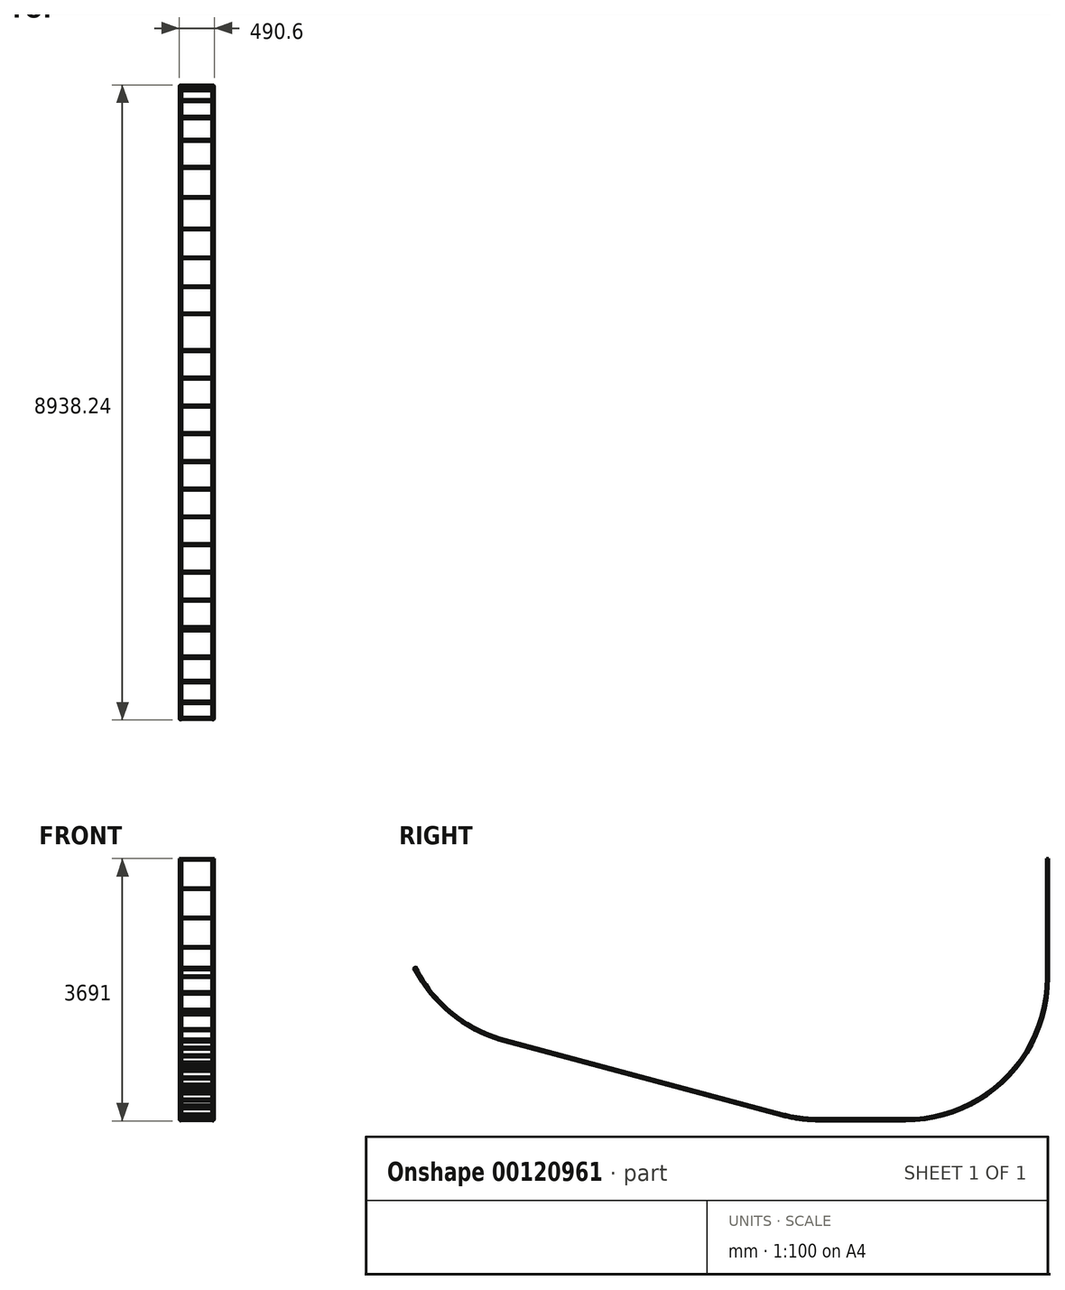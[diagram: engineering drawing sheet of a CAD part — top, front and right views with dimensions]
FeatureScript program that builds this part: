
annotation { "Feature Type Name" : "Feature", "Feature Type Description" : "" }
export const myFeature = defineFeature(function(context is Context, id is Id, definition is map)
    precondition{}
    {
        {
            var Q0;
            Q0=qCreatedBy(makeId("Right.planeOp"),FACE);
            var sketch = newSketch(context, id + "F0", { "sketchPlane" : qUnion([Q0])});
            skLineSegment(sketch, "E0", {"start": v(0, 0) * mm, "end": v(0, 1981.2) * mm, "construction": true});
            skLineSegment(sketch, "E1", {"start": v(0, 0) * mm, "end": v(-1981.2, 0) * mm, "construction": true});
            skArc(sketch, "E2", {"start": v(0, 1981.2) * mm, "mid": v(-580.28, 580.28) * mm, "end": v(-1981.2, 0) * mm});
            skLineSegment(sketch, "E3", {"start": v(0, 1981.2) * mm, "end": v(0, 3657.6) * mm});
            skLineSegment(sketch, "E4", {"start": v(-1981.2, 0) * mm, "end": v(-3200.4, 0) * mm});
            skArc(sketch, "E5", {"start": v(-3200.4, 0) * mm, "mid": v(-3459, 16.95) * mm, "end": v(-3713.17, 67.5) * mm});
            skLineSegment(sketch, "E6", {"start": v(-3713.17, 67.5) * mm, "end": v(-7620, 1114.34) * mm});
            skArc(sketch, "E7", {"start": v(-7620, 1114.34) * mm, "mid": v(-8356.22, 1490.12) * mm, "end": v(-8875.04, 2133.6) * mm});
            skLineSegment(sketch, "E8", {"start": v(-3200.4, 0) * mm, "end": v(-7620, 0) * mm, "construction": true});
            skSolve(sketch);
        }
        {
            var Q0;
            Q0=sQuery(id+"F0.wireOp",VERTEX,"E3.end");
            var Q1;
            Q1=qCreatedBy(makeId("Top.planeOp"),FACE);
            cPlane(context, id + "F1", {"entities" : qUnion([Q0, Q1]), "cplaneType" : CPlaneType.PLANE_POINT, "offset" : 25.4 * mm, "width" : 152.4 * mm, "height" : 152.4 * mm});
        }
        {
            var Q0;
            Q0=qCreatedBy(id+"F1.planeOp",FACE);
            var sketch = newSketch(context, id + "F2", { "sketchPlane" : qUnion([Q0])});
            skCircle(sketch, "E9", {"center": v(0, 16.7) * mm, "radius": 16.7 * mm});
            skCircle(sketch, "E10", {"center": v(0, 16.7) * mm, "radius": 13.32 * mm});
            skSolve(sketch);
        }
        {
            var Q0;
            Q0=makeQuery(id+"F2.imprint","IMPRINT",FACE,{"disambiguationData":[TD([[makeQuery(id+"F2.imprint","IMPRINT",EDGE,{"derivedFrom":sQuery(id+"F2.wireOp",EDGE,"E9")}),1.0]])]});
            var Q1;
            Q1=sQuery(id+"F0.wireOp",EDGE,"E3");
            var Q2;
            Q2=sQuery(id+"F0.wireOp",EDGE,"E2");
            var Q3;
            Q3=sQuery(id+"F0.wireOp",EDGE,"E4");
            var Q4;
            Q4=sQuery(id+"F0.wireOp",EDGE,"E5");
            var Q5;
            Q5=sQuery(id+"F0.wireOp",EDGE,"E6");
            var Q6;
            Q6=sQuery(id+"F0.wireOp",EDGE,"E7");
            sweep(context, id + "F3", {"profiles" : qUnion([Q0]), "path" : qUnion([Q1, Q2, Q3, Q4, Q5, Q6])});
        }
        {
            var Q0;
            Q0=qCreatedBy(makeId("Right.planeOp"),FACE);
            cPlane(context, id + "F4", {"entities" : qUnion([Q0]), "cplaneType" : CPlaneType.OFFSET, "offset" : 228.6 * mm, "oppositeDirection" : true, "width" : 152.4 * mm, "height" : 152.4 * mm});
        }
        {
            var Q0;
            Q0=qCreatedBy(id+"F4.planeOp",FACE);
            var sketch = newSketch(context, id + "F5", { "sketchPlane" : qUnion([Q0])});
            skLineSegment(sketch, "E11.0", {"start": v(0, 1981.2) * mm, "end": v(0, 3657.6) * mm, "construction": true});
            skArc(sketch, "E12.0", {"start": v(0, 1981.2) * mm, "mid": v(-580.28, 580.28) * mm, "end": v(-1981.2, 0) * mm, "construction": true});
            skLineSegment(sketch, "E13", {"start": v(-3200.4, 0) * mm, "end": v(-1981.2, 0) * mm, "construction": true});
            skArc(sketch, "E14.0", {"start": v(-3200.4, 0) * mm, "mid": v(-3459, 16.95) * mm, "end": v(-3713.17, 67.5) * mm, "construction": true});
            skLineSegment(sketch, "E15.0", {"start": v(-3713.17, 67.5) * mm, "end": v(-7620, 1114.34) * mm, "construction": true});
            skArc(sketch, "E16.0", {"start": v(-7620, 1114.34) * mm, "mid": v(-8356.22, 1490.12) * mm, "end": v(-8875.04, 2133.6) * mm, "construction": true});
            skArc(sketch, "E17.0", {"start": v(-7624.32, 1098.2) * mm, "mid": v(-8366.75, 1477.16) * mm, "end": v(-8889.94, 2126.06) * mm, "construction": true});
            skLineSegment(sketch, "E17.1", {"start": v(-3717.5, 51.38) * mm, "end": v(-7624.32, 1098.2) * mm, "construction": true});
            skLineSegment(sketch, "E17.2", {"start": v(16.7, 1981.2) * mm, "end": v(16.7, 3657.6) * mm, "construction": true});
            skArc(sketch, "E17.3", {"start": v(16.7, 1981.2) * mm, "mid": v(-568.47, 568.47) * mm, "end": v(-1981.2, -16.7) * mm, "construction": true});
            skLineSegment(sketch, "E17.4", {"start": v(-3200.4, -16.7) * mm, "end": v(-1981.2, -16.7) * mm, "construction": true});
            skArc(sketch, "E17.5", {"start": v(-3200.4, -16.7) * mm, "mid": v(-3461.18, 0.4) * mm, "end": v(-3717.5, 51.38) * mm, "construction": true});
            skLineSegment(sketch, "E18.bottom", {"start": v(4, 3657.6) * mm, "end": v(29.4, 3657.6) * mm});
            skLineSegment(sketch, "E18.top", {"start": v(4, 3632.2) * mm, "end": v(29.4, 3632.2) * mm});
            skLineSegment(sketch, "E18.left", {"start": v(4, 3657.6) * mm, "end": v(4, 3632.2) * mm});
            skLineSegment(sketch, "E18.right", {"start": v(29.4, 3657.6) * mm, "end": v(29.4, 3632.2) * mm});
            skPoint(sketch, "E18.middle", {"position": v(16.7, 3644.9) * mm});
            skLineSegment(sketch, "E19.0.1.0", {"start": v(4, 3219.45) * mm, "end": v(29.4, 3219.45) * mm});
            skLineSegment(sketch, "E19.0.1.1", {"start": v(4, 3244.85) * mm, "end": v(4, 3219.45) * mm});
            skPoint(sketch, "E19.0.1.2", {"position": v(16.7, 3232.15) * mm});
            skLineSegment(sketch, "E19.0.1.3", {"start": v(4, 3244.85) * mm, "end": v(29.4, 3244.85) * mm});
            skLineSegment(sketch, "E19.0.1.4", {"start": v(29.4, 3244.85) * mm, "end": v(29.4, 3219.45) * mm});
            skLineSegment(sketch, "E19.0.2.0", {"start": v(4, 2806.7) * mm, "end": v(29.4, 2806.7) * mm});
            skLineSegment(sketch, "E19.0.2.1", {"start": v(4, 2832.1) * mm, "end": v(4, 2806.7) * mm});
            skPoint(sketch, "E19.0.2.2", {"position": v(16.7, 2819.4) * mm});
            skLineSegment(sketch, "E19.0.2.3", {"start": v(4, 2832.1) * mm, "end": v(29.4, 2832.1) * mm});
            skLineSegment(sketch, "E19.0.2.4", {"start": v(29.4, 2832.1) * mm, "end": v(29.4, 2806.7) * mm});
            skLineSegment(sketch, "E19.0.3.0", {"start": v(4, 2393.95) * mm, "end": v(29.4, 2393.95) * mm});
            skLineSegment(sketch, "E19.0.3.1", {"start": v(4, 2419.35) * mm, "end": v(4, 2393.95) * mm});
            skPoint(sketch, "E19.0.3.2", {"position": v(16.7, 2406.65) * mm});
            skLineSegment(sketch, "E19.0.3.3", {"start": v(4, 2419.35) * mm, "end": v(29.4, 2419.35) * mm});
            skLineSegment(sketch, "E19.0.3.4", {"start": v(29.4, 2419.35) * mm, "end": v(29.4, 2393.95) * mm});
            skLineSegment(sketch, "E19.0.4.0", {"start": v(4, 1981.2) * mm, "end": v(29.4, 1981.2) * mm});
            skLineSegment(sketch, "E19.0.4.1", {"start": v(4, 2006.6) * mm, "end": v(4, 1981.2) * mm});
            skPoint(sketch, "E19.0.4.2", {"position": v(16.7, 1993.9) * mm});
            skLineSegment(sketch, "E19.0.4.3", {"start": v(4, 2006.6) * mm, "end": v(29.4, 2006.6) * mm});
            skLineSegment(sketch, "E19.0.4.4", {"start": v(29.4, 2006.6) * mm, "end": v(29.4, 1981.2) * mm});
            skLineSegment(sketch, "E19.direction1", {"start": v(4, 3632.2) * mm, "end": v(29.4, 3632.2) * mm, "construction": true});
            skLineSegment(sketch, "E19.direction2", {"start": v(4, 3632.2) * mm, "end": v(4, 3219.45) * mm, "construction": true});
            skLineSegment(sketch, "E20", {"start": v(4, 1981.2) * mm, "end": v(3.84, 1955.8) * mm});
            skLineSegment(sketch, "E21", {"start": v(3.84, 1955.8) * mm, "end": v(29.24, 1955.64) * mm});
            skLineSegment(sketch, "E22", {"start": v(29.24, 1955.64) * mm, "end": v(29.4, 1981.04) * mm});
            skLineSegment(sketch, "E23", {"start": v(29.4, 1981.04) * mm, "end": v(4, 1981.2) * mm});
            skLineSegment(sketch, "E24", {"start": v(16.7, 1981.12) * mm, "end": v(16.54, 1955.72) * mm, "construction": true});
            skLineSegment(sketch, "E25.1.0", {"start": v(-21.05, 1533.64) * mm, "end": v(-45.77, 1539.45) * mm});
            skLineSegment(sketch, "E25.1.1", {"start": v(-26.86, 1508.91) * mm, "end": v(-21.05, 1533.64) * mm});
            skLineSegment(sketch, "E25.1.2", {"start": v(-51.58, 1514.72) * mm, "end": v(-26.86, 1508.91) * mm});
            skLineSegment(sketch, "E25.1.3", {"start": v(-45.77, 1539.45) * mm, "end": v(-51.58, 1514.72) * mm});
            skLineSegment(sketch, "E25.2.0", {"start": v(-169.78, 1108.69) * mm, "end": v(-192.6, 1119.85) * mm});
            skLineSegment(sketch, "E25.2.1", {"start": v(-180.95, 1085.87) * mm, "end": v(-169.78, 1108.69) * mm});
            skLineSegment(sketch, "E25.2.2", {"start": v(-203.76, 1097.04) * mm, "end": v(-180.95, 1085.87) * mm});
            skLineSegment(sketch, "E25.2.3", {"start": v(-192.6, 1119.85) * mm, "end": v(-203.76, 1097.04) * mm});
            skLineSegment(sketch, "E25.3.0", {"start": v(-409.35, 727.48) * mm, "end": v(-429.1, 743.45) * mm});
            skLineSegment(sketch, "E25.3.1", {"start": v(-425.31, 707.73) * mm, "end": v(-409.35, 727.48) * mm});
            skLineSegment(sketch, "E25.3.2", {"start": v(-445.07, 723.7) * mm, "end": v(-425.31, 707.73) * mm});
            skLineSegment(sketch, "E25.3.3", {"start": v(-429.1, 743.45) * mm, "end": v(-445.07, 723.7) * mm});
            skLineSegment(sketch, "E25.4.0", {"start": v(-727.74, 409.15) * mm, "end": v(-743.45, 429.1) * mm});
            skLineSegment(sketch, "E25.4.1", {"start": v(-747.7, 393.44) * mm, "end": v(-727.74, 409.15) * mm});
            skLineSegment(sketch, "E25.4.2", {"start": v(-763.4, 413.4) * mm, "end": v(-747.7, 393.44) * mm});
            skLineSegment(sketch, "E25.4.3", {"start": v(-743.45, 429.1) * mm, "end": v(-763.4, 413.4) * mm});
            skLineSegment(sketch, "E25.5.0", {"start": v(-1108.98, 169.64) * mm, "end": v(-1119.85, 192.6) * mm});
            skLineSegment(sketch, "E25.5.1", {"start": v(-1131.93, 158.77) * mm, "end": v(-1108.98, 169.64) * mm});
            skLineSegment(sketch, "E25.5.2", {"start": v(-1142.8, 181.72) * mm, "end": v(-1131.93, 158.77) * mm});
            skLineSegment(sketch, "E25.5.3", {"start": v(-1119.85, 192.6) * mm, "end": v(-1142.8, 181.72) * mm});
            skLineSegment(sketch, "E25.6.0", {"start": v(-1533.96, 20.97) * mm, "end": v(-1539.45, 45.77) * mm});
            skLineSegment(sketch, "E25.6.1", {"start": v(-1558.76, 15.48) * mm, "end": v(-1533.96, 20.97) * mm});
            skLineSegment(sketch, "E25.6.2", {"start": v(-1564.25, 40.28) * mm, "end": v(-1558.76, 15.48) * mm});
            skLineSegment(sketch, "E25.6.3", {"start": v(-1539.45, 45.77) * mm, "end": v(-1564.25, 40.28) * mm});
            skLineSegment(sketch, "E25.7.0", {"start": v(-1981.36, -29.4) * mm, "end": v(-1981.2, -4) * mm});
            skLineSegment(sketch, "E25.7.1", {"start": v(-2006.76, -29.24) * mm, "end": v(-1981.36, -29.4) * mm});
            skLineSegment(sketch, "E25.7.2", {"start": v(-2006.6, -3.84) * mm, "end": v(-2006.76, -29.24) * mm});
            skLineSegment(sketch, "E25.7.3", {"start": v(-1981.2, -4) * mm, "end": v(-2006.6, -3.84) * mm});
            skLineSegment(sketch, "E25.anchor1", {"start": v(-1981.2, 1981.2) * mm, "end": v(4, 1981.2) * mm, "construction": true});
            skLineSegment(sketch, "E25.anchor2", {"start": v(-1981.2, 1981.2) * mm, "end": v(-1981.2, -4) * mm, "construction": true});
            skLineSegment(sketch, "E26.bottom", {"start": v(-2413, -4) * mm, "end": v(-2387.6, -4) * mm});
            skLineSegment(sketch, "E26.top", {"start": v(-2413, -29.4) * mm, "end": v(-2387.6, -29.4) * mm});
            skLineSegment(sketch, "E26.left", {"start": v(-2413, -4) * mm, "end": v(-2413, -29.4) * mm});
            skLineSegment(sketch, "E26.right", {"start": v(-2387.6, -4) * mm, "end": v(-2387.6, -29.4) * mm});
            skPoint(sketch, "E26.middle", {"position": v(-2400.3, -16.7) * mm});
            skLineSegment(sketch, "E27.1.0.0", {"start": v(-2819.4, -29.4) * mm, "end": v(-2794, -29.4) * mm});
            skPoint(sketch, "E27.1.0.1", {"position": v(-2806.7, -16.7) * mm});
            skLineSegment(sketch, "E27.1.0.2", {"start": v(-2794, -4) * mm, "end": v(-2794, -29.4) * mm});
            skLineSegment(sketch, "E27.1.0.3", {"start": v(-2819.4, -4) * mm, "end": v(-2819.4, -29.4) * mm});
            skLineSegment(sketch, "E27.1.0.4", {"start": v(-2819.4, -4) * mm, "end": v(-2794, -4) * mm});
            skLineSegment(sketch, "E27.2.0.0", {"start": v(-3225.8, -29.4) * mm, "end": v(-3200.4, -29.4) * mm});
            skPoint(sketch, "E27.2.0.1", {"position": v(-3213.1, -16.7) * mm});
            skLineSegment(sketch, "E27.2.0.2", {"start": v(-3200.4, -4) * mm, "end": v(-3200.4, -29.4) * mm});
            skLineSegment(sketch, "E27.2.0.3", {"start": v(-3225.8, -4) * mm, "end": v(-3225.8, -29.4) * mm});
            skLineSegment(sketch, "E27.2.0.4", {"start": v(-3225.8, -4) * mm, "end": v(-3200.4, -4) * mm});
            skLineSegment(sketch, "E27.direction1", {"start": v(-2413, -29.4) * mm, "end": v(-2819.4, -29.4) * mm, "construction": true});
            skLineSegment(sketch, "E28", {"start": v(-3713.17, 67.5) * mm, "end": v(-3717.5, 51.38) * mm, "construction": true});
            skLineSegment(sketch, "E29", {"start": v(-3714.2, 63.64) * mm, "end": v(-3720.78, 39.1) * mm});
            skLineSegment(sketch, "E30", {"start": v(-3720.78, 39.1) * mm, "end": v(-3696.25, 32.54) * mm});
            skLineSegment(sketch, "E31", {"start": v(-3696.25, 32.54) * mm, "end": v(-3689.67, 57.07) * mm});
            skLineSegment(sketch, "E32", {"start": v(-3689.67, 57.07) * mm, "end": v(-3714.2, 63.64) * mm});
            skLineSegment(sketch, "E33", {"start": v(-3717.5, 51.38) * mm, "end": v(-3692.96, 44.8) * mm, "construction": true});
            skLineSegment(sketch, "E34", {"start": v(-3714.2, 63.64) * mm, "end": v(-4104.3, 168.17) * mm});
            skLineSegment(sketch, "E35", {"start": v(-4104.3, 168.17) * mm, "end": v(-4110.88, 143.64) * mm});
            skLineSegment(sketch, "E36", {"start": v(-4110.88, 143.64) * mm, "end": v(-4086.35, 137.06) * mm});
            skLineSegment(sketch, "E37", {"start": v(-4086.35, 137.06) * mm, "end": v(-4079.77, 161.6) * mm});
            skLineSegment(sketch, "E38", {"start": v(-4079.77, 161.6) * mm, "end": v(-4104.3, 168.17) * mm});
            skLineSegment(sketch, "E39", {"start": v(-4104.3, 168.17) * mm, "end": v(-4494.4, 272.7) * mm});
            skLineSegment(sketch, "E40", {"start": v(-4494.4, 272.7) * mm, "end": v(-4500.98, 248.16) * mm});
            skLineSegment(sketch, "E41", {"start": v(-4500.98, 248.16) * mm, "end": v(-4476.44, 241.59) * mm});
            skLineSegment(sketch, "E42", {"start": v(-4476.44, 241.59) * mm, "end": v(-4469.87, 266.12) * mm});
            skLineSegment(sketch, "E43", {"start": v(-4469.87, 266.12) * mm, "end": v(-4494.4, 272.7) * mm});
            skLineSegment(sketch, "E44", {"start": v(-4494.4, 272.7) * mm, "end": v(-4884.5, 377.22) * mm});
            skLineSegment(sketch, "E45", {"start": v(-4884.5, 377.22) * mm, "end": v(-4891.08, 352.69) * mm});
            skLineSegment(sketch, "E46", {"start": v(-4891.08, 352.69) * mm, "end": v(-4866.54, 346.12) * mm});
            skLineSegment(sketch, "E47", {"start": v(-4866.54, 346.12) * mm, "end": v(-4859.97, 370.65) * mm});
            skLineSegment(sketch, "E48", {"start": v(-4859.97, 370.65) * mm, "end": v(-4884.5, 377.22) * mm});
            skLineSegment(sketch, "E49", {"start": v(-4884.5, 377.22) * mm, "end": v(-5274.6, 481.75) * mm});
            skLineSegment(sketch, "E50", {"start": v(-5274.6, 481.75) * mm, "end": v(-5281.18, 457.22) * mm});
            skLineSegment(sketch, "E51", {"start": v(-5281.18, 457.22) * mm, "end": v(-5256.64, 450.64) * mm});
            skLineSegment(sketch, "E52", {"start": v(-5256.64, 450.64) * mm, "end": v(-5250.07, 475.18) * mm});
            skLineSegment(sketch, "E53", {"start": v(-5250.07, 475.18) * mm, "end": v(-5274.6, 481.75) * mm});
            skLineSegment(sketch, "E54", {"start": v(-5274.6, 481.75) * mm, "end": v(-5664.7, 586.28) * mm});
            skLineSegment(sketch, "E55", {"start": v(-5664.7, 586.28) * mm, "end": v(-5671.28, 561.74) * mm});
            skLineSegment(sketch, "E56", {"start": v(-5671.28, 561.74) * mm, "end": v(-5646.74, 555.17) * mm});
            skLineSegment(sketch, "E57", {"start": v(-5646.74, 555.17) * mm, "end": v(-5640.17, 579.7) * mm});
            skLineSegment(sketch, "E58", {"start": v(-5640.17, 579.7) * mm, "end": v(-5664.7, 586.28) * mm});
            skLineSegment(sketch, "E59", {"start": v(-5664.7, 586.28) * mm, "end": v(-6054.8, 690.8) * mm});
            skLineSegment(sketch, "E60", {"start": v(-6054.8, 690.8) * mm, "end": v(-6061.37, 666.27) * mm});
            skLineSegment(sketch, "E61", {"start": v(-6061.37, 666.27) * mm, "end": v(-6036.84, 659.7) * mm});
            skLineSegment(sketch, "E62", {"start": v(-6036.84, 659.7) * mm, "end": v(-6030.27, 684.23) * mm});
            skLineSegment(sketch, "E63", {"start": v(-6030.27, 684.23) * mm, "end": v(-6054.8, 690.8) * mm});
            skLineSegment(sketch, "E64", {"start": v(-6054.8, 690.8) * mm, "end": v(-6444.9, 795.33) * mm});
            skLineSegment(sketch, "E65", {"start": v(-6444.9, 795.33) * mm, "end": v(-6451.47, 770.8) * mm});
            skLineSegment(sketch, "E66", {"start": v(-6451.47, 770.8) * mm, "end": v(-6426.94, 764.22) * mm});
            skLineSegment(sketch, "E67", {"start": v(-6426.94, 764.22) * mm, "end": v(-6420.36, 788.76) * mm});
            skLineSegment(sketch, "E68", {"start": v(-6420.36, 788.76) * mm, "end": v(-6444.9, 795.33) * mm});
            skLineSegment(sketch, "E69", {"start": v(-6444.9, 795.33) * mm, "end": v(-6835, 899.86) * mm});
            skLineSegment(sketch, "E70", {"start": v(-6835, 899.86) * mm, "end": v(-6841.57, 875.32) * mm});
            skLineSegment(sketch, "E71", {"start": v(-6841.57, 875.32) * mm, "end": v(-6817.04, 868.75) * mm});
            skLineSegment(sketch, "E72", {"start": v(-6817.04, 868.75) * mm, "end": v(-6810.46, 893.28) * mm});
            skLineSegment(sketch, "E73", {"start": v(-6810.46, 893.28) * mm, "end": v(-6835, 899.86) * mm});
            skLineSegment(sketch, "E74", {"start": v(-6835, 899.86) * mm, "end": v(-7225.1, 1004.38) * mm});
            skLineSegment(sketch, "E75", {"start": v(-7225.1, 1004.38) * mm, "end": v(-7231.67, 979.85) * mm});
            skLineSegment(sketch, "E76", {"start": v(-7231.67, 979.85) * mm, "end": v(-7207.14, 973.27) * mm});
            skLineSegment(sketch, "E77", {"start": v(-7207.14, 973.27) * mm, "end": v(-7200.56, 997.8) * mm});
            skLineSegment(sketch, "E78", {"start": v(-7200.56, 997.8) * mm, "end": v(-7225.1, 1004.38) * mm});
            skLineSegment(sketch, "E79", {"start": v(-7225.1, 1004.38) * mm, "end": v(-7615.2, 1108.91) * mm});
            skLineSegment(sketch, "E80", {"start": v(-7615.2, 1108.91) * mm, "end": v(-7621.77, 1084.38) * mm});
            skLineSegment(sketch, "E81", {"start": v(-7621.77, 1084.38) * mm, "end": v(-7597.24, 1077.8) * mm});
            skLineSegment(sketch, "E82", {"start": v(-7597.24, 1077.8) * mm, "end": v(-7590.66, 1102.34) * mm});
            skLineSegment(sketch, "E83", {"start": v(-7590.66, 1102.34) * mm, "end": v(-7615.2, 1108.91) * mm});
            skLineSegment(sketch, "E84.MirrorCS", {"start": v(-3175, -4) * mm, "end": v(-3200.4, -4) * mm});
            skLineSegment(sketch, "E85.MirrorCS", {"start": v(-3175, -4) * mm, "end": v(-3175, -29.4) * mm});
            skLineSegment(sketch, "E86.MirrorCS", {"start": v(-3175, -29.4) * mm, "end": v(-3200.4, -29.4) * mm});
            skPoint(sketch, "E87.MirrorP", {"position": v(-3187.7, -16.7) * mm});
            skLineSegment(sketch, "E88", {"start": v(-7620.96, 1110.45) * mm, "end": v(-7627.69, 1085.96) * mm});
            skLineSegment(sketch, "E89", {"start": v(-7627.69, 1085.96) * mm, "end": v(-7652.18, 1092.7) * mm});
            skLineSegment(sketch, "E90", {"start": v(-7652.18, 1092.7) * mm, "end": v(-7645.45, 1117.18) * mm});
            skLineSegment(sketch, "E91", {"start": v(-7645.45, 1117.18) * mm, "end": v(-7620.96, 1110.45) * mm});
            skLineSegment(sketch, "E92", {"start": v(-7624.32, 1098.2) * mm, "end": v(-7648.81, 1104.94) * mm, "construction": true});
            skLineSegment(sketch, "E93.1.0", {"start": v(-8003.01, 1256.42) * mm, "end": v(-8014.62, 1233.83) * mm});
            skLineSegment(sketch, "E93.1.1", {"start": v(-8008.81, 1245.13) * mm, "end": v(-8031.4, 1256.73) * mm, "construction": true});
            skLineSegment(sketch, "E93.1.2", {"start": v(-8025.6, 1268.03) * mm, "end": v(-8003.01, 1256.42) * mm});
            skLineSegment(sketch, "E93.1.3", {"start": v(-8037.21, 1245.44) * mm, "end": v(-8025.6, 1268.03) * mm});
            skLineSegment(sketch, "E93.1.4", {"start": v(-8014.62, 1233.83) * mm, "end": v(-8037.21, 1245.44) * mm});
            skLineSegment(sketch, "E93.2.0", {"start": v(-8347.04, 1477.59) * mm, "end": v(-8363.03, 1457.85) * mm});
            skLineSegment(sketch, "E93.2.1", {"start": v(-8355.04, 1467.72) * mm, "end": v(-8374.77, 1483.7) * mm, "construction": true});
            skLineSegment(sketch, "E93.2.2", {"start": v(-8366.78, 1493.58) * mm, "end": v(-8347.04, 1477.59) * mm});
            skLineSegment(sketch, "E93.2.3", {"start": v(-8382.77, 1473.84) * mm, "end": v(-8366.78, 1493.58) * mm});
            skLineSegment(sketch, "E93.2.4", {"start": v(-8363.03, 1457.85) * mm, "end": v(-8382.77, 1473.84) * mm});
            skLineSegment(sketch, "E93.3.0", {"start": v(-8638.45, 1764.56) * mm, "end": v(-8658.15, 1748.52) * mm});
            skLineSegment(sketch, "E93.3.1", {"start": v(-8648.3, 1756.54) * mm, "end": v(-8664.34, 1776.23) * mm, "construction": true});
            skLineSegment(sketch, "E93.3.2", {"start": v(-8654.5, 1784.25) * mm, "end": v(-8638.45, 1764.56) * mm});
            skLineSegment(sketch, "E93.3.3", {"start": v(-8674.19, 1768.21) * mm, "end": v(-8654.5, 1784.25) * mm});
            skLineSegment(sketch, "E93.3.4", {"start": v(-8658.15, 1748.52) * mm, "end": v(-8674.19, 1768.21) * mm});
            skLineSegment(sketch, "E93.4.0", {"start": v(-8864.87, 2105.16) * mm, "end": v(-8887.44, 2093.5) * mm});
            skLineSegment(sketch, "E93.4.1", {"start": v(-8876.16, 2099.32) * mm, "end": v(-8887.82, 2121.89) * mm, "construction": true});
            skLineSegment(sketch, "E93.4.2", {"start": v(-8876.54, 2127.72) * mm, "end": v(-8864.87, 2105.16) * mm});
            skLineSegment(sketch, "E93.4.3", {"start": v(-8899.1, 2116.05) * mm, "end": v(-8876.54, 2127.72) * mm});
            skLineSegment(sketch, "E93.4.4", {"start": v(-8887.44, 2093.5) * mm, "end": v(-8899.1, 2116.05) * mm});
            skLineSegment(sketch, "E93.anchor1", {"start": v(-7107.23, 3028.03) * mm, "end": v(-7652.18, 1092.7) * mm, "construction": true});
            skLineSegment(sketch, "E93.anchor2", {"start": v(-7107.23, 3028.03) * mm, "end": v(-8899.1, 2116.05) * mm, "construction": true});
            skSolve(sketch);
        }
        {
            var Q0;
            Q0=makeQuery(id+"F5.imprint","IMPRINT",FACE,{"disambiguationData":[TD([[makeQuery(id+"F5.imprint","IMPRINT",EDGE,{"derivedFrom":sQuery(id+"F5.wireOp",EDGE,"E18.bottom")}),-1.0]])]});
            var Q1;
            Q1=makeQuery(id+"F5.imprint","IMPRINT",FACE,{"disambiguationData":[TD([[makeQuery(id+"F5.imprint","IMPRINT",EDGE,{"derivedFrom":sQuery(id+"F5.wireOp",EDGE,"E19.0.1.0")}),1.0]])]});
            var Q2;
            Q2=makeQuery(id+"F5.imprint","IMPRINT",FACE,{"disambiguationData":[TD([[makeQuery(id+"F5.imprint","IMPRINT",EDGE,{"derivedFrom":sQuery(id+"F5.wireOp",EDGE,"E19.0.2.0")}),1.0]])]});
            var Q3;
            Q3=makeQuery(id+"F5.imprint","IMPRINT",FACE,{"disambiguationData":[TD([[makeQuery(id+"F5.imprint","IMPRINT",EDGE,{"derivedFrom":sQuery(id+"F5.wireOp",EDGE,"E19.0.3.0")}),1.0]])]});
            var Q4;
            {var subQ0=sQuery(id+"F5.wireOp",EDGE,"E19.0.4.1");Q4=makeQuery(id+"F5.imprint","IMPRINT",FACE,{"disambiguationData":[TD([[makeQuery(id+"F5.imprint","IMPRINT",EDGE,{"derivedFrom":subQ0}),1.0]])]});}
            var Q5;
            Q5=makeQuery(id+"F5.imprint","IMPRINT",FACE,{"disambiguationData":[TD([[makeQuery(id+"F5.imprint","IMPRINT",EDGE,{"derivedFrom":sQuery(id+"F5.wireOp",EDGE,"E25.1.0")}),1.0]])]});
            var Q6;
            Q6=makeQuery(id+"F5.imprint","IMPRINT",FACE,{"disambiguationData":[TD([[makeQuery(id+"F5.imprint","IMPRINT",EDGE,{"derivedFrom":sQuery(id+"F5.wireOp",EDGE,"E25.2.0")}),1.0]])]});
            var Q7;
            Q7=makeQuery(id+"F5.imprint","IMPRINT",FACE,{"disambiguationData":[TD([[makeQuery(id+"F5.imprint","IMPRINT",EDGE,{"derivedFrom":sQuery(id+"F5.wireOp",EDGE,"E25.3.0")}),1.0]])]});
            var Q8;
            Q8=makeQuery(id+"F5.imprint","IMPRINT",FACE,{"disambiguationData":[TD([[makeQuery(id+"F5.imprint","IMPRINT",EDGE,{"derivedFrom":sQuery(id+"F5.wireOp",EDGE,"E25.4.0")}),1.0]])]});
            var Q9;
            Q9=makeQuery(id+"F5.imprint","IMPRINT",FACE,{"disambiguationData":[TD([[makeQuery(id+"F5.imprint","IMPRINT",EDGE,{"derivedFrom":sQuery(id+"F5.wireOp",EDGE,"E25.5.0")}),1.0]])]});
            var Q10;
            Q10=makeQuery(id+"F5.imprint","IMPRINT",FACE,{"disambiguationData":[TD([[makeQuery(id+"F5.imprint","IMPRINT",EDGE,{"derivedFrom":sQuery(id+"F5.wireOp",EDGE,"E25.6.0")}),1.0]])]});
            var Q11;
            Q11=makeQuery(id+"F5.imprint","IMPRINT",FACE,{"disambiguationData":[TD([[makeQuery(id+"F5.imprint","IMPRINT",EDGE,{"derivedFrom":sQuery(id+"F5.wireOp",EDGE,"E25.7.0")}),1.0]])]});
            var Q12;
            Q12=makeQuery(id+"F5.imprint","IMPRINT",FACE,{"disambiguationData":[TD([[makeQuery(id+"F5.imprint","IMPRINT",EDGE,{"derivedFrom":sQuery(id+"F5.wireOp",EDGE,"E26.bottom")}),-1.0]])]});
            var Q13;
            Q13=makeQuery(id+"F5.imprint","IMPRINT",FACE,{"disambiguationData":[TD([[makeQuery(id+"F5.imprint","IMPRINT",EDGE,{"derivedFrom":sQuery(id+"F5.wireOp",EDGE,"E27.1.0.0")}),1.0]])]});
            var Q14;
            Q14=makeQuery(id+"F5.imprint","IMPRINT",FACE,{"disambiguationData":[TD([[makeQuery(id+"F5.imprint","IMPRINT",EDGE,{"derivedFrom":sQuery(id+"F5.wireOp",EDGE,"E27.2.0.2")}),1.0]])]});
            var Q15;
            Q15=makeQuery(id+"F5.imprint","IMPRINT",FACE,{"disambiguationData":[TD([[makeQuery(id+"F5.imprint","IMPRINT",EDGE,{"derivedFrom":sQuery(id+"F5.wireOp",EDGE,"E29")}),1.0]])]});
            var Q16;
            Q16=makeQuery(id+"F5.imprint","IMPRINT",FACE,{"disambiguationData":[TD([[makeQuery(id+"F5.imprint","IMPRINT",EDGE,{"derivedFrom":sQuery(id+"F5.wireOp",EDGE,"E35")}),1.0]])]});
            var Q17;
            Q17=makeQuery(id+"F5.imprint","IMPRINT",FACE,{"disambiguationData":[TD([[makeQuery(id+"F5.imprint","IMPRINT",EDGE,{"derivedFrom":sQuery(id+"F5.wireOp",EDGE,"E40")}),1.0]])]});
            var Q18;
            Q18=makeQuery(id+"F5.imprint","IMPRINT",FACE,{"disambiguationData":[TD([[makeQuery(id+"F5.imprint","IMPRINT",EDGE,{"derivedFrom":sQuery(id+"F5.wireOp",EDGE,"E45")}),1.0]])]});
            var Q19;
            Q19=makeQuery(id+"F5.imprint","IMPRINT",FACE,{"disambiguationData":[TD([[makeQuery(id+"F5.imprint","IMPRINT",EDGE,{"derivedFrom":sQuery(id+"F5.wireOp",EDGE,"E50")}),1.0]])]});
            var Q20;
            Q20=makeQuery(id+"F5.imprint","IMPRINT",FACE,{"disambiguationData":[TD([[makeQuery(id+"F5.imprint","IMPRINT",EDGE,{"derivedFrom":sQuery(id+"F5.wireOp",EDGE,"E55")}),1.0]])]});
            var Q21;
            Q21=makeQuery(id+"F5.imprint","IMPRINT",FACE,{"disambiguationData":[TD([[makeQuery(id+"F5.imprint","IMPRINT",EDGE,{"derivedFrom":sQuery(id+"F5.wireOp",EDGE,"E60")}),1.0]])]});
            var Q22;
            Q22=makeQuery(id+"F5.imprint","IMPRINT",FACE,{"disambiguationData":[TD([[makeQuery(id+"F5.imprint","IMPRINT",EDGE,{"derivedFrom":sQuery(id+"F5.wireOp",EDGE,"E65")}),1.0]])]});
            var Q23;
            Q23=makeQuery(id+"F5.imprint","IMPRINT",FACE,{"disambiguationData":[TD([[makeQuery(id+"F5.imprint","IMPRINT",EDGE,{"derivedFrom":sQuery(id+"F5.wireOp",EDGE,"E70")}),1.0]])]});
            var Q24;
            Q24=makeQuery(id+"F5.imprint","IMPRINT",FACE,{"disambiguationData":[TD([[makeQuery(id+"F5.imprint","IMPRINT",EDGE,{"derivedFrom":sQuery(id+"F5.wireOp",EDGE,"E75")}),1.0]])]});
            var Q25;
            Q25=makeQuery(id+"F5.imprint","IMPRINT",FACE,{"disambiguationData":[TD([[makeQuery(id+"F5.imprint","IMPRINT",EDGE,{"derivedFrom":sQuery(id+"F5.wireOp",EDGE,"E80")}),1.0]])]});
            var Q26;
            Q26=makeQuery(id+"F5.imprint","IMPRINT",FACE,{"disambiguationData":[TD([[makeQuery(id+"F5.imprint","IMPRINT",EDGE,{"derivedFrom":sQuery(id+"F5.wireOp",EDGE,"E88")}),-1.0]])]});
            var Q27;
            Q27=makeQuery(id+"F5.imprint","IMPRINT",FACE,{"disambiguationData":[TD([[makeQuery(id+"F5.imprint","IMPRINT",EDGE,{"derivedFrom":sQuery(id+"F5.wireOp",EDGE,"E93.1.0")}),-1.0]])]});
            var Q28;
            Q28=makeQuery(id+"F5.imprint","IMPRINT",FACE,{"disambiguationData":[TD([[makeQuery(id+"F5.imprint","IMPRINT",EDGE,{"derivedFrom":sQuery(id+"F5.wireOp",EDGE,"E93.2.0")}),-1.0]])]});
            var Q29;
            Q29=makeQuery(id+"F5.imprint","IMPRINT",FACE,{"disambiguationData":[TD([[makeQuery(id+"F5.imprint","IMPRINT",EDGE,{"derivedFrom":sQuery(id+"F5.wireOp",EDGE,"E93.3.0")}),-1.0]])]});
            var Q30;
            Q30=makeQuery(id+"F5.imprint","IMPRINT",FACE,{"disambiguationData":[TD([[makeQuery(id+"F5.imprint","IMPRINT",EDGE,{"derivedFrom":sQuery(id+"F5.wireOp",EDGE,"E93.4.0")}),-1.0]])]});
            var Q31;
            Q31=makeQuery(id+"F3.opSweep","SWEPT_FACE",FACE,{"disambiguationData":[OSD([sQuery(id+"F0.wireOp",EDGE,"E3"),sQuery(id+"F2.wireOp",EDGE,"E9")])]});
            extrude(context, id + "F6", {"entities" : qUnion([Q0, Q1, Q2, Q3, Q4, Q5, Q6, Q7, Q8, Q9, Q10, Q11, Q12, Q13, Q14, Q15, Q16, Q17, Q18, Q19, Q20, Q21, Q22, Q23, Q24, Q25, Q26, Q27, Q28, Q29, Q30]), "operationType" : NewBodyOperationType.ADD, "endBoundEntityFace" : qUnion([Q31]), "depth" : 228.6 * mm});
        }
        {
            var Q0;
            Q0=makeQuery(id+"F3.opSweep","SWEPT_BODY",BODY,{"disambiguationData":[OSD([sQuery(id+"F0.wireOp",EDGE,"E7"),sQuery(id+"F2.wireOp",EDGE,"E9"),sQuery(id+"F2.wireOp",EDGE,"E10")])]});
            var Q1;
            Q1=qCreatedBy(id+"F4.planeOp",FACE);
            mirror(context, id + "F7", {"operationType" : NewBodyOperationType.ADD, "entities" : qUnion([Q0]), "mirrorPlane" : qUnion([Q1])});
        }
    });
